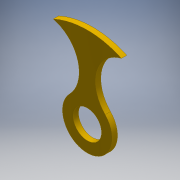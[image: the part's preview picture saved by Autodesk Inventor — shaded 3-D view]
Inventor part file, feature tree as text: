
AUTODESK INVENTOR PART (.ipt)
format: ipt  version: 2016 (Build 200138000, 138)  size: 110,592 bytes
history: native  units: mm
features: extrude x1, sketch x1
ambient origin geometry x8: Origin, YZ Plane, XZ Plane, XY Plane, X Axis, Y Axis, Z Axis, Center Point
bodies: Body1 (feature_tree)
feature tree (2):
  extrude  "Extrusion3"  Depth=9.6mm
  sketch  "Sketch1"  dims[d0=8.0mm d1=14.0mm d2=46.0mm d11=1.5mm d12=0.0mm d15=9.6mm d17=4.6mm]
